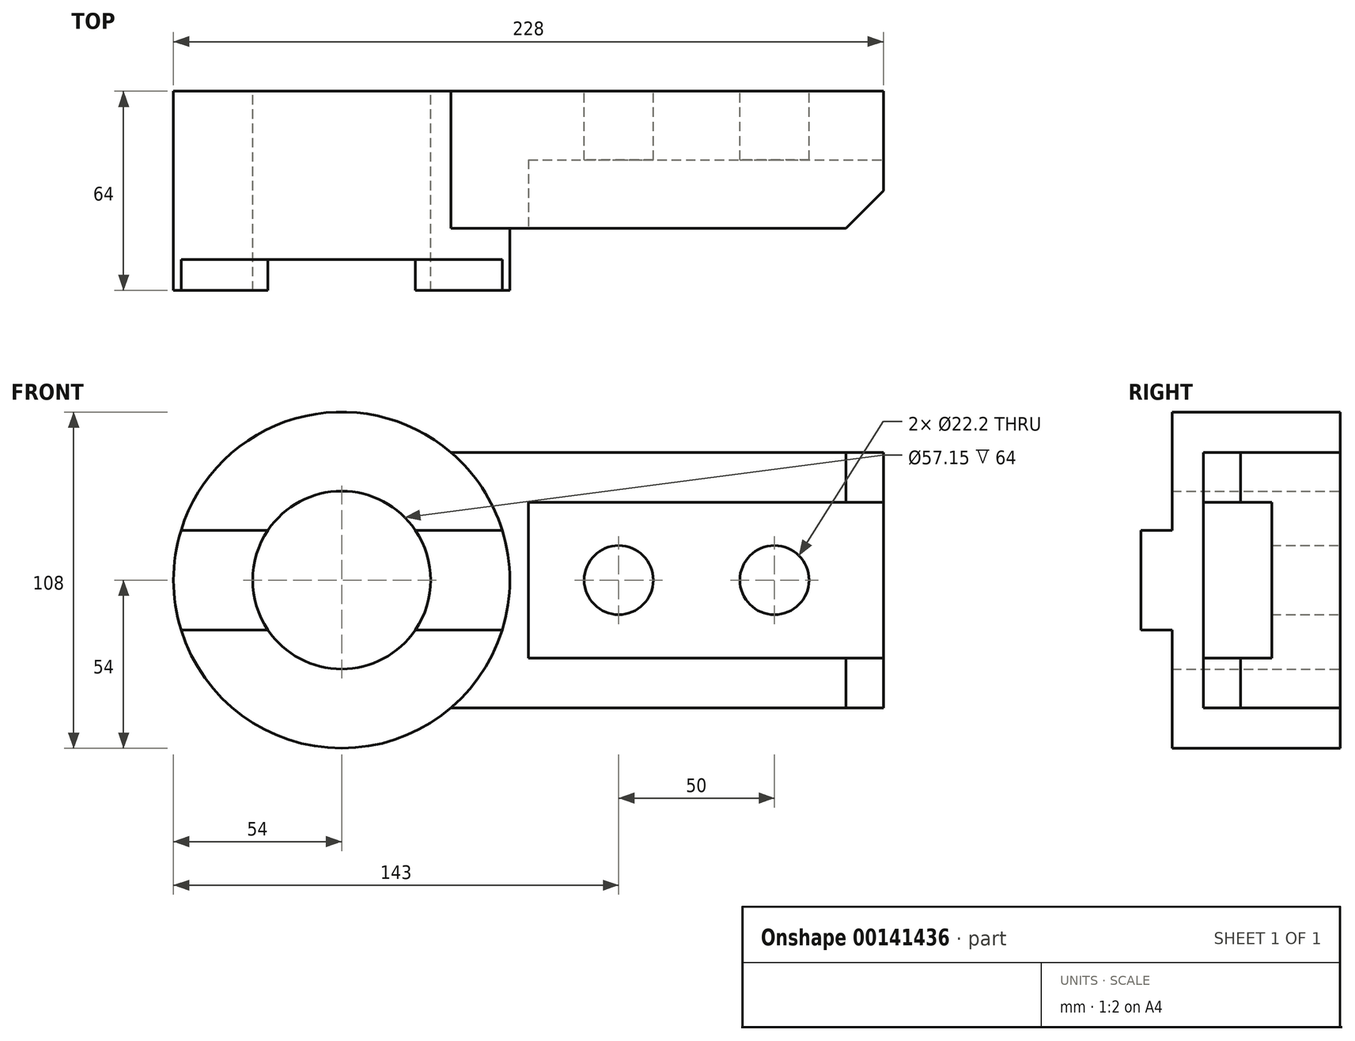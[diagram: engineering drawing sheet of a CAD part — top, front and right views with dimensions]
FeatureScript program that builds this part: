
annotation { "Feature Type Name" : "Feature", "Feature Type Description" : "" }
export const myFeature = defineFeature(function(context is Context, id is Id, definition is map)
    precondition{}
    {
        {
            var Q0;
            Q0=qCreatedBy(makeId("Front.planeOp"),FACE);
            var sketch = newSketch(context, id + "F0", { "sketchPlane" : qUnion([Q0])});
            skCircle(sketch, "E0", {"center": v(0, 0) * mm, "radius": 28.57 * mm});
            skCircle(sketch, "E1", {"center": v(0, 0) * mm, "radius": 54 * mm});
            skLineSegment(sketch, "E2", {"start": v(35.14, 41) * mm, "end": v(174, 41) * mm});
            skLineSegment(sketch, "E3", {"start": v(174, 41) * mm, "end": v(174, -41) * mm});
            skLineSegment(sketch, "E4", {"start": v(174, -41) * mm, "end": v(35.14, -41) * mm});
            skLineSegment(sketch, "E5", {"start": v(-91.67, 0) * mm, "end": v(317.32, 0) * mm, "construction": true});
            skCircle(sketch, "E6", {"center": v(89, 0) * mm, "radius": 11.1 * mm});
            skCircle(sketch, "E7", {"center": v(139, 0) * mm, "radius": 11.1 * mm});
            skSolve(sketch);
        }
        {
            var Q0;
            {var subQ1=sQuery(id+"F0.wireOp",EDGE,"E2");Q0=makeQuery(id+"F0.imprint","IMPRINT",FACE,{"disambiguationData":[TD([[makeQuery(id+"F0.imprint","IMPRINT",EDGE,{"derivedFrom":subQ1}),-1.0]])]});}
            extrude(context, id + "F1", {"entities" : qUnion([Q0]), "depth" : 44 * mm});
        }
        {
            var Q0;
            Q0=makeQuery(id+"F0.imprint","IMPRINT",FACE,{"disambiguationData":[TD([[makeQuery(id+"F0.imprint","IMPRINT",EDGE,{"derivedFrom":sQuery(id+"F0.wireOp",EDGE,"E0")}),-1.0]])]});
            extrude(context, id + "F2", {"entities" : qUnion([Q0]), "operationType" : NewBodyOperationType.ADD, "depth" : 64 * mm});
        }
        {
            var Q0;
            Q0=makeQuery(id+"F1.opExtrude","SWEPT_FACE",FACE,{"disambiguationData":[OSD([sQuery(id+"F0.wireOp",EDGE,"E2")])]});
            var sketch = newSketch(context, id + "F3", { "sketchPlane" : qUnion([Q0])});
            skLineSegment(sketch, "E8", {"start": v(174, -32) * mm, "end": v(162, -44) * mm});
            skLineSegment(sketch, "E9", {"start": v(162, -44) * mm, "end": v(174, -44) * mm});
            skLineSegment(sketch, "E10", {"start": v(174, -44) * mm, "end": v(174, -32) * mm});
            skSolve(sketch);
        }
        {
            var Q0;
            Q0 = qSketchRegion(id + "F3", true);
            extrude(context, id + "F4", {"entities" : qUnion([Q0]), "operationType" : NewBodyOperationType.REMOVE, "endBound" : BoundingType.THROUGH_ALL, "oppositeDirection" : true, "depth" : 25 * mm});
        }
        {
            var Q0;
            Q0=makeQuery(id+"F1.opExtrude","CAP_FACE",FACE,{"disambiguationData":[OSD([sQuery(id+"F0.wireOp",EDGE,"E1"),sQuery(id+"F0.wireOp",EDGE,"E2"),sQuery(id+"F0.wireOp",EDGE,"E3"),sQuery(id+"F0.wireOp",EDGE,"E4"),sQuery(id+"F0.wireOp",EDGE,"E6"),sQuery(id+"F0.wireOp",EDGE,"E7")])],"isStart":false});
            var sketch = newSketch(context, id + "F5", { "sketchPlane" : qUnion([Q0])});
            skLineSegment(sketch, "E11.bottom", {"start": v(60, 25) * mm, "end": v(174, 25) * mm});
            skLineSegment(sketch, "E11.top", {"start": v(60, -25) * mm, "end": v(174, -25) * mm});
            skLineSegment(sketch, "E11.left", {"start": v(60, 25) * mm, "end": v(60, -25) * mm});
            skLineSegment(sketch, "E11.right", {"start": v(174, 25) * mm, "end": v(174, -25) * mm});
            skSolve(sketch);
        }
        {
            var Q0;
            Q0 = qSketchRegion(id + "F5", true);
            extrude(context, id + "F6", {"entities" : qUnion([Q0]), "operationType" : NewBodyOperationType.REMOVE, "oppositeDirection" : true, "depth" : 22 * mm});
        }
        {
            var Q0;
            Q0=makeQuery(id+"F2.opExtrude","CAP_FACE",FACE,{"disambiguationData":[OSD([sQuery(id+"F0.wireOp",EDGE,"E0"),sQuery(id+"F0.wireOp",EDGE,"E1")])],"isStart":false});
            var sketch = newSketch(context, id + "F7", { "sketchPlane" : qUnion([Q0])});
            skLineSegment(sketch, "E12", {"start": v(-51.58, 16) * mm, "end": v(51.58, 16) * mm});
            skLineSegment(sketch, "E13", {"start": v(-51.58, -16) * mm, "end": v(51.58, -16) * mm});
            skArc(sketch, "E14", {"start": v(-51.58, 16) * mm, "mid": v(-54, 0) * mm, "end": v(-51.58, -16) * mm});
            skArc(sketch, "E15", {"start": v(51.58, -16) * mm, "mid": v(54, 0) * mm, "end": v(51.58, 16) * mm});
            skSolve(sketch);
        }
        {
            var Q0;
            {var subQ0=sQuery(id+"F7.wireOp",EDGE,"E12");var subQ3=makeQuery(id+"F2.opExtrude","CAP_EDGE",EDGE,{"disambiguationData":[OSD([sQuery(id+"F0.wireOp",EDGE,"E0")])],"isStart":false});var subQ4=makeQuery(id+"F7.imprint","INTERSECT",VERTEX,{"disambiguationData":[OD(0.0)],"derivedFrom":[subQ3,subQ0]});Q0=makeQuery(id+"F7.imprint","IMPRINT",FACE,{"disambiguationData":[TD([[makeQuery(id+"F7.imprint","IMPRINT",EDGE,{"disambiguationData":[TD([[subQ4,1.0]])],"derivedFrom":subQ3}),-1.0]])]});}
            var Q1;
            {var subQ0=sQuery(id+"F7.wireOp",EDGE,"E13");var subQ3=makeQuery(id+"F2.opExtrude","CAP_EDGE",EDGE,{"disambiguationData":[OSD([sQuery(id+"F0.wireOp",EDGE,"E0")])],"isStart":false});var subQ4=makeQuery(id+"F7.imprint","INTERSECT",VERTEX,{"disambiguationData":[OD(0.0)],"derivedFrom":[subQ3,subQ0]});Q1=makeQuery(id+"F7.imprint","IMPRINT",FACE,{"disambiguationData":[TD([[makeQuery(id+"F7.imprint","IMPRINT",EDGE,{"disambiguationData":[TD([[subQ4,-1.0]])],"derivedFrom":subQ3}),-1.0]])]});}
            extrude(context, id + "F8", {"entities" : qUnion([Q0, Q1]), "operationType" : NewBodyOperationType.REMOVE, "oppositeDirection" : true, "depth" : 10 * mm});
        }
    });
